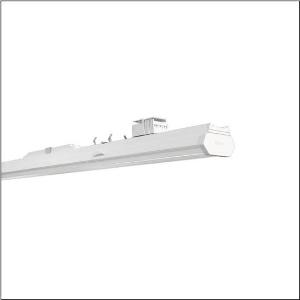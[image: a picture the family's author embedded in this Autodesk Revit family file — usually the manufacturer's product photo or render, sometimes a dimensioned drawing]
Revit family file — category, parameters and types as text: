
# Revit family: licross_r__21_protected_ho_52td13mn4fxs_5700
name_source: partatom
category: Lighting Fixtures
units: mm (PartAtom-declared; Revit-internal decimal feet)

## family parameters
Cut with Voids When Loaded = No
Host = Face
Light Source = No
Part Type = Normal
Room Calculation Point = No
Round Connector Dimension = Use Diameter
Shared = No

## types (1)
- --- (1 x LED, 15060 lm, 83.2 W, 4000K)
    Apparent Load = 83 VA
    CIE Flux Codes = 89 96 99 100 99
    Color Rendering = 80
    Color Temperature = 4000K
    Default Elevation = 1800 mm
    Description = Licross® 21 Protected HO, luminaire insert, of sheet steel, galvanised, coil coated, white, length: 1.500mm, width: 66mm, height: 67mm, LED rated luminous flux: 15.060lm, light colour: 840, control gear: ON/OFF Multilumen, with plug, 3-pole, with phase selection, mains connection: 220..240V, AC, 50/60Hz, rated input power: 83W, halogen-free wiring, primary light control with lens, of plastic, primary optical cover: cover, of PMMA, light emission: direct distribution, primary light characteristic: symmetric, protection rating (complete): IP54, insulation class (complete): insulation class I (protective earthing), certification: CE, ENEC, VDE, UKCA, protection symbol: D if used in an environment with non-conductive dust loads with corresponding accessories, impact resistance: IK06, permissible ambient temperature for indoor applications: -35..+35°C, corresponds to IFS (International Featured Standards) requirements for safety and quality in the food industry, reducing of maximum allowable ambient temperature of 5°C with ceiling mounting, LABS conformity tested according to VDMA 24364:2018-05, packaging unit: 1 piece
    Height = 92 mm
    Lamp = 1 x LED
    Lamp Light Flux = 15060 lm
    Lamp Power = 83.2 W
    Lamp count = 1
    Length = 1500 mm
    Luminous efficacy = 181 lm/W
    Manufacturer = Siteco
    ModVariant = No
    Model = 52TD13MN4FXS
    Mounting Place = Ceiling
    Mounting Type = Pendant
    Number of Poles = 1
    OnlyDefault = Yes
    Power Factor = 1
    Product Name = Licross® 21 Protected HO
    Product group = luminaire insert
    ProductGroupID = 901
    Protection Class = Protection class I
    Protection Degree = IP 54
    RLX_Detail_Level = 1
    RLX_Emergency_Light_Flux = 0 lm
    RLX_Emergency_Type = 0
    RLX_Emergency_Type_DB = No
    RlxData = <blob elided: 21921 chars, md5=75baedcf>
    Socket = socket
    Standby Power = 0 W
    System Light Flux = 15060 lm
    System Power = 83 W
    Type Comments = factory setting: luminous flux: 100 % | (A | C | E) | 195 mA
    Type Image = l_1256148.jpg
    URL = http://relux.com
    VarID = @adj_057331
    Voltage = 0 V
    Weight = 0.00 kg
    Width = 88 mm

## geometry (parser evidence)
native form markers: Blend x4, Sweep x9
no freeform markers — native parametric forms only
